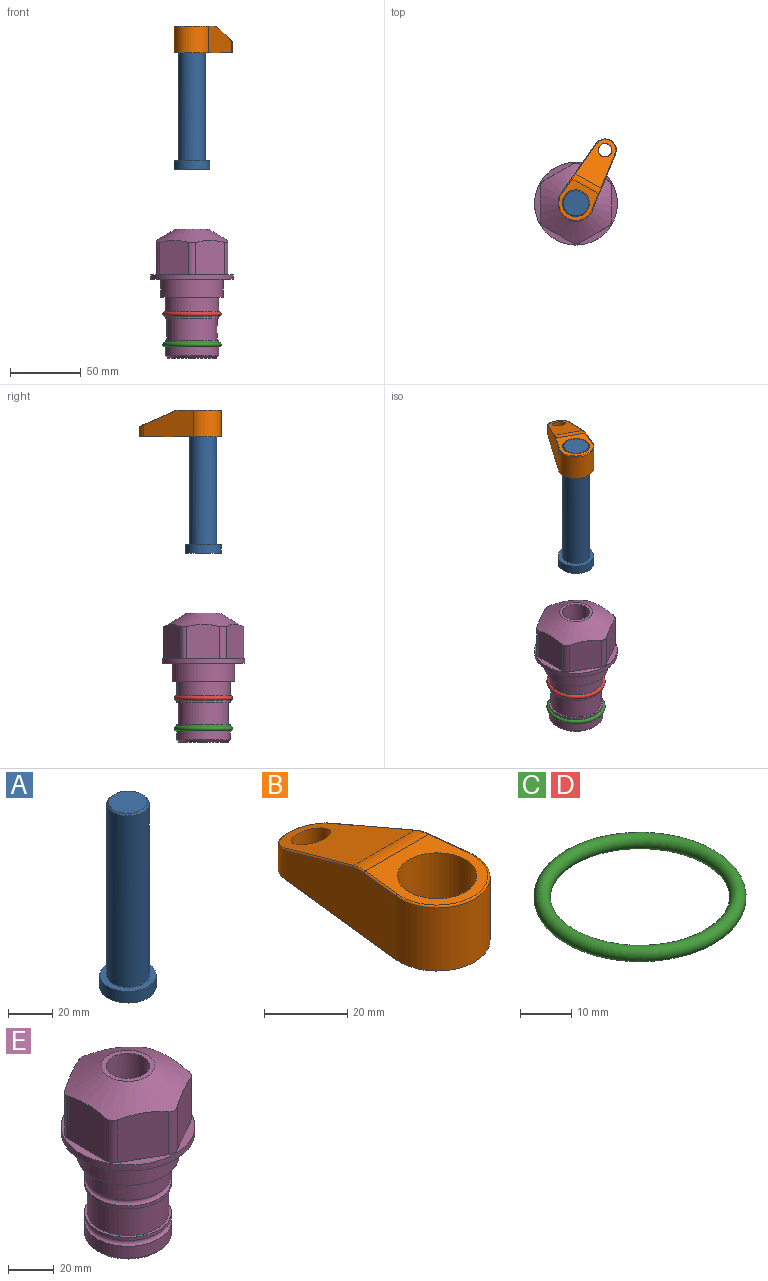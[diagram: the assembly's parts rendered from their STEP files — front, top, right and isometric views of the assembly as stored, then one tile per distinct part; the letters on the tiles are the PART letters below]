
ASSEMBLY  parts=5 mates=3
PART A: 6 faces, bbox 25.4x25.4x101.6 mm
  f0: plane 17.46x17.46mm, normal (0,0,1), area 239.5mm2, adj f5
  f1: plane 25.4x25.4mm, normal (0,0,-1), area 506.7mm2, adj f2
  f2: cylinder r=12.7mm len=25.4mm, axis (0,0,1), area 506.7mm2, adj f1,f3
  f3: plane 25.4x25.4mm, normal (0,0,1), area 221.7mm2, adj f2,f4
  f4: cylinder r=9.53mm len=94.46mm, axis (0,0,1), area 5653mm2, adj f3,f5
  f5: cone r=8.73mm half-angle=45deg, axis (0,0,-1), area 64.4mm2, adj f0,f4
PART B: 44 faces, bbox 27.5x64.5x19.1 mm
  f0: plane 2.3x0.95mm, normal (0,0,-1), area 1mm2, adj f25,f30,f34
  f1: plane 63.5x25.4mm, normal (0,0,-1), area 561.7mm2, adj f2,f3,f4,f5,f6,f7,f19,f20
  f2: cylinder r=12.7mm len=25.4mm, axis (0,0,-1), area 792.2mm2, adj f1,f3,f5,f13
  f3: plane 42.33x18.54mm, normal (0.99,0.11,0), area 647mm2, adj f1,f2,f4,f11,f12,f14
  f4: cylinder r=7.94mm len=15.78mm, axis (0,0,-1), area 158.6mm2, adj f1,f3,f5,f16
  f5: plane 42.33x18.54mm, normal (-0.99,0.11,0), area 647mm2, adj f1,f2,f4,f15,f17,f18
  f6: cylinder r=9.53mm len=19.05mm, axis (0,0,-1), area 1140.1mm2, adj f1,f8
  f7: cylinder r=4.76mm len=10.98mm, axis (0,0,-1), area 276.1mm2, adj f1,f9
  f8: plane 25.83x24.38mm, normal (0,0,1), area 262.2mm2, adj f6,f10,f11,f13,f15
  f9: plane 32.49x20.55mm, normal (0,0.34,0.94), area 489.9mm2, adj f7,f10,f14,f16,f18
  f10: cylinder r=12.7mm len=21.49mm, axis (-1,0,0), area 93.2mm2, adj f8,f9,f12,f17
  f11: cylinder r=0.51mm len=12.34mm, axis (0.11,-0.99,0), area 9.9mm2, adj f3,f8,f12,f13
  f12: bspline ~7.62x1.64mm, area 3.5mm2, adj f3,f10,f11,f14
  f13: torus R=12.19mm, axis (0,0,1), area 33.6mm2, adj f2,f8,f11,f15
  f14: cylinder r=0.51mm len=26.01mm, axis (0.1,-0.93,0.34), area 21.6mm2, adj f3,f9,f12,f16
  f15: cylinder r=0.51mm len=12.34mm, axis (0.11,0.99,0), area 9.9mm2, adj f5,f8,f13,f17
  f16: bspline ~15.78x7.05mm, area 15.7mm2, adj f4,f9,f14,f18
  f17: bspline ~7.62x1.64mm, area 3.5mm2, adj f5,f10,f15,f18
  f18: cylinder r=0.51mm len=26.01mm, axis (0.1,0.93,-0.34), area 21.6mm2, adj f5,f9,f16,f17
  f19: plane 21.6x14.29mm, normal (-0.99,-0.11,0), area 242.6mm2, adj f1,f26,f28,f34,f36,f38
  f20: plane 21.6x14.29mm, normal (0.99,-0.11,0), area 242.6mm2, adj f1,f27,f29,f37,f39,f41
  f21: cylinder r=12.7mm len=14.29mm, axis (0,0,-1), area 173.2mm2, adj f1,f26,f27,f30,f31,f33
  f22: cylinder r=7.94mm len=7.63mm, axis (0,0,-1), area 53.8mm2, adj f1,f28,f29,f42
  f23: plane 2.3x0.95mm, normal (0,0,-1), area 1mm2, adj f25,f33,f37
  f24: plane 17.94x12.32mm, normal (0,-0.34,-0.94), area 191.2mm2, adj f25,f38,f41,f42
  f25: cylinder r=9.53mm len=12.93mm, axis (-1,0,0), area 37.5mm2, adj f0,f23,f24,f31,f36,f39
  f26: cylinder r=1.59mm len=14.29mm, axis (0,0,-1), area 49mm2, adj f1,f19,f21,f32
  f27: cylinder r=1.59mm len=14.29mm, axis (0,0,-1), area 49mm2, adj f1,f20,f21,f35
  f28: cylinder r=1.59mm len=7.28mm, axis (0,0,-1), area 22.1mm2, adj f1,f19,f22,f40
  f29: cylinder r=1.59mm len=7.28mm, axis (0,0,-1), area 22.1mm2, adj f1,f20,f22,f43
  f30: torus R=14.29mm, axis (0,0,1), area 5.8mm2, adj f0,f21,f31,f32
  f31: bspline ~11.06x2.73mm, area 20.8mm2, adj f21,f25,f30,f33
  f32: sphere r=1.59mm, area 5.4mm2, adj f26,f30,f34
  f33: torus R=14.29mm, axis (0,0,1), area 5.8mm2, adj f21,f23,f31,f35
  f34: cylinder r=1.59mm len=1.68mm, axis (-0.11,0.99,0), area 2.4mm2, adj f0,f19,f32,f36
  f35: sphere r=1.59mm, area 5.4mm2, adj f27,f33,f37
  f36: bspline ~5.82x2.33mm, area 7.7mm2, adj f19,f25,f34,f38
  f37: cylinder r=1.59mm len=1.68mm, axis (0.11,0.99,0), area 2.4mm2, adj f20,f23,f35,f39
  f38: cylinder r=1.59mm len=18.33mm, axis (0.1,-0.93,0.34), area 46.7mm2, adj f19,f24,f36,f40
  f39: bspline ~5.82x2.33mm, area 7.7mm2, adj f20,f25,f37,f41
  f40: sphere r=1.59mm, area 3.6mm2, adj f28,f38,f42
  f41: cylinder r=1.59mm len=18.33mm, axis (0.1,0.93,-0.34), area 46.7mm2, adj f20,f24,f39,f43
  f42: bspline ~8.31x1.84mm, area 15.3mm2, adj f22,f24,f40,f43
  f43: sphere r=1.59mm, area 3.6mm2, adj f29,f41,f42
PART C: 1 faces, bbox 44.7x44.7x3.2 mm
  f0: torus R=19.05mm, axis (0,0,1), area 1193.9mm2
PART D: same geometry as C
PART E: 36 faces, bbox 58.7x58.7x91.2 mm
  f0: cylinder r=17.78mm len=35.56mm, axis (0,0,1), area 1670.8mm2, adj f23,f24,f31
  f1: cylinder r=19.05mm len=38.1mm, axis (0,0,1), area 1191.9mm2, adj f26,f27,f30
  f2: plane 58.66x58.66mm, normal (0,0,-1), area 1150.6mm2, adj f3,f28
  f3: cylinder r=29.33mm len=58.66mm, axis (0,0,-1), area 585.1mm2, adj f2,f4
  f4: plane 58.66x58.66mm, normal (0,0,1), area 475.9mm2, adj f3,f5,f6,f7,f8,f9,f10,f11
  f5: plane 24.5x20.32mm, normal (-0.5,0.87,0), area 562.8mm2, adj f4,f15,f16,f17
  f6: plane 24.5x20.32mm, normal (0.5,0.87,0), area 562.8mm2, adj f4,f14,f15,f17
  f7: plane 24.5x23.48mm, normal (1,0,0), area 562.8mm2, adj f4,f13,f14,f17
  f8: plane 24.5x20.32mm, normal (0.5,-0.87,0), area 562.8mm2, adj f4,f12,f13,f17
  f9: plane 24.5x20.32mm, normal (-0.5,-0.87,0), area 562.8mm2, adj f4,f11,f12,f17
  f10: plane 24.5x23.48mm, normal (-1,0,0), area 562.8mm2, adj f4,f11,f16,f17
  f11: cylinder r=5.08mm len=23.01mm, axis (0,0,-1), area 121.2mm2, adj f4,f9,f10,f17
  f12: cylinder r=5.08mm len=23.01mm, axis (0,0,-1), area 121.2mm2, adj f4,f8,f9,f17
  f13: cylinder r=5.08mm len=23.01mm, axis (0,0,-1), area 121.2mm2, adj f4,f7,f8,f17
  f14: cylinder r=5.08mm len=23.01mm, axis (0,0,-1), area 121.2mm2, adj f4,f6,f7,f17
  f15: cylinder r=5.08mm len=23.01mm, axis (0,0,-1), area 121.2mm2, adj f4,f5,f6,f17
  f16: cylinder r=5.08mm len=23.01mm, axis (0,0,-1), area 121.2mm2, adj f4,f5,f10,f17
  f17: cone r=11.73mm half-angle=60deg, axis (0,0,-1), area 2071.8mm2, adj f5,f6,f7,f8,f9,f10,f11,f12
  f18: plane 23.46x23.46mm, normal (0,0,1), area 147.4mm2, adj f17,f35
  f19: plane 34.93x34.93mm, normal (0,0,-1), area 958mm2, adj f29
  f20: cylinder r=19.05mm len=38.1mm, axis (0,0,1), area 760.1mm2, adj f21,f29
  f21: torus R=19.05mm, axis (0,0,1), area 565.3mm2, adj f20,f22
  f22: cylinder r=19.05mm len=38.1mm, axis (0,0,1), area 190mm2, adj f21,f23
  f23: plane 38.1x38.1mm, normal (0,0,1), area 146.9mm2, adj f0,f22
  f24: plane 38.1x38.1mm, normal (0,0,-1), area 146.9mm2, adj f0,f25
  f25: cylinder r=19.05mm len=38.1mm, axis (0,0,1), area 190mm2, adj f24,f26
  f26: torus R=19.05mm, axis (0,0,1), area 565.3mm2, adj f1,f25
  f27: plane 44.45x44.45mm, normal (0,0,-1), area 411.7mm2, adj f1,f28
  f28: cylinder r=22.23mm len=44.45mm, axis (0,0,1), area 1773.5mm2, adj f2,f27
  f29: cone r=19.05mm half-angle=45deg, axis (0,0,1), area 257.5mm2, adj f19,f20
  f30: cylinder r=3.17mm len=6.75mm, axis (-1,0,0), area 128mm2, adj f1,f33
  f31: cylinder r=3.17mm len=6.35mm, axis (-1,0,0), area 102.5mm2, adj f0,f33
  f32: plane 25.4x25.4mm, normal (0,0,1), area 506.7mm2, adj f33
  f33: cylinder r=12.7mm len=66.42mm, axis (0,0,-1), area 5236.2mm2, adj f30,f31,f32,f34
  f34: cone r=9.53mm half-angle=30deg, axis (0,0,-1), area 443.4mm2, adj f33,f35
  f35: cylinder r=9.53mm len=19.05mm, axis (0,0,-1), area 849mm2, adj f18,f34
PLACE A rot(axis=(0,0,1),61.2deg) t=(0,0,105.86)mm
PLACE B rot(axis=(0,0,-1),28.8deg) t=(0,0,160.47)mm
PLACE C t=(0,0,-21.59)mm
PLACE D at identity
PLACE E at identity fixed
MATE fastened C.f0 <-> E.f0  axis (0,0,1) through (0,0,-46.1)mm
MATE cylindrical A.f2 <-> E.f0  axis (0,0,1) through (0,0,131.5)mm
MATE fastened B.f2 <-> A.f2  axis (0,0,1) through (0,0,179.52)mm
